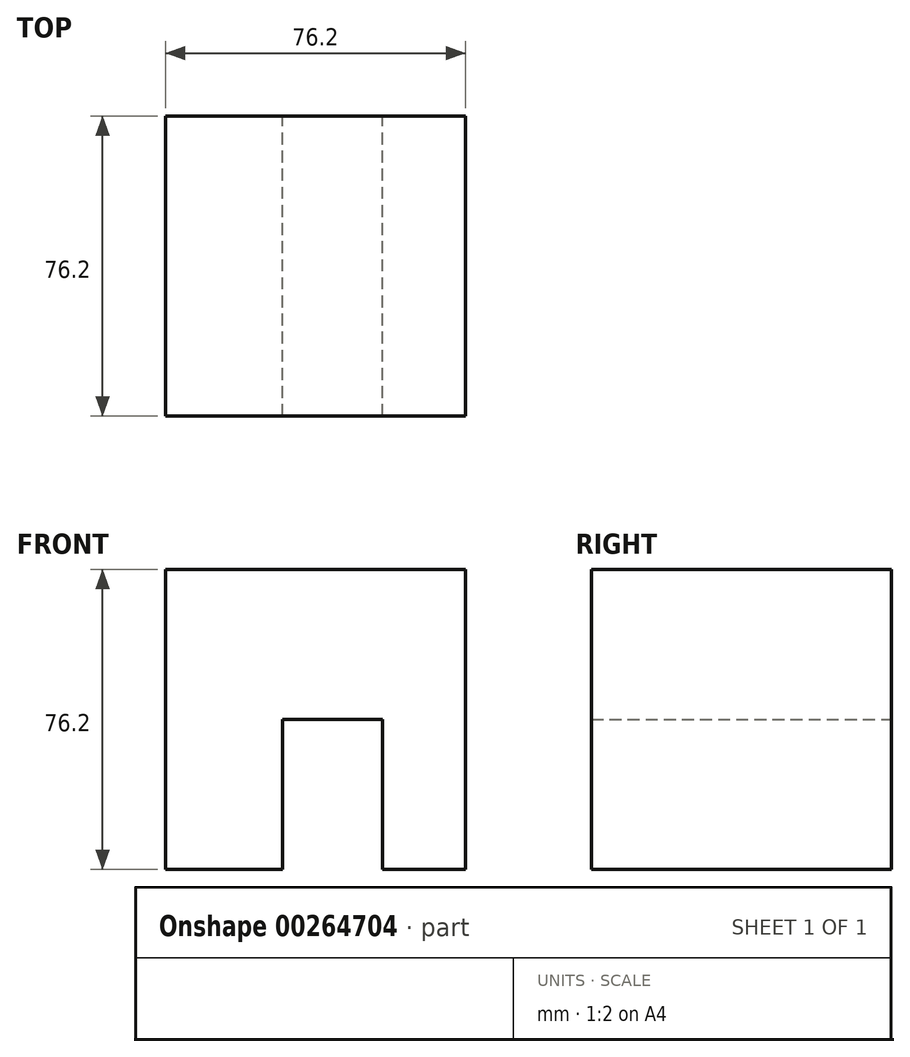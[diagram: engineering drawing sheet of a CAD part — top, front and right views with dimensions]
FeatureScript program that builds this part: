
annotation { "Feature Type Name" : "Feature", "Feature Type Description" : "" }
export const myFeature = defineFeature(function(context is Context, id is Id, definition is map)
    precondition{}
    {
        {
            var Q0;
            Q0=qCreatedBy(makeId("Front.planeOp"),FACE);
            var sketch = newSketch(context, id + "F0", { "sketchPlane" : qUnion([Q0])});
            skLineSegment(sketch, "E0.bottom", {"start": v(0, 0) * mm, "end": v(-76.2, 0) * mm});
            skLineSegment(sketch, "E0.top", {"start": v(0, 76.2) * mm, "end": v(-76.2, 76.2) * mm});
            skLineSegment(sketch, "E0.left", {"start": v(0, 0) * mm, "end": v(0, 76.2) * mm});
            skLineSegment(sketch, "E0.right", {"start": v(-76.2, 0) * mm, "end": v(-76.2, 76.2) * mm});
            skSolve(sketch);
        }
        {
            var Q0;
            Q0 = qSketchRegion(id + "F0", true);
            extrude(context, id + "F1", {"entities" : qUnion([Q0]), "depth" : 76.2 * mm});
        }
        {
            var Q0;
            Q0=qCreatedBy(makeId("Front.planeOp"),FACE);
            var sketch = newSketch(context, id + "F2", { "sketchPlane" : qUnion([Q0])});
            skLineSegment(sketch, "E1", {"start": v(-21.11, 0) * mm, "end": v(-21.11, 38.1) * mm});
            skLineSegment(sketch, "E2", {"start": v(-21.11, 38.1) * mm, "end": v(-46.51, 38.1) * mm});
            skLineSegment(sketch, "E3", {"start": v(-46.51, 38.1) * mm, "end": v(-46.51, 0) * mm});
            skLineSegment(sketch, "E4", {"start": v(-46.51, 0) * mm, "end": v(-21.11, 0) * mm});
            skSolve(sketch);
        }
        {
            var Q0;
            Q0 = qSketchRegion(id + "F2", true);
            extrude(context, id + "F3", {"entities" : qUnion([Q0]), "operationType" : NewBodyOperationType.REMOVE, "depth" : 76.2 * mm});
        }
    });
